# Revit family: Lighting-Troffer-Current-CBT2
name_source: partatom
category: Lighting Fixtures
units: mm (PartAtom-declared; Revit-internal decimal feet)

## family parameters
Cut with Voids When Loaded = No
Host = Face
Light Source = Yes
OmniClass Number = 23.80.70.11
OmniClass Title = Luminaries for Internal Lighting
Part Type = Normal
Room Calculation Point = No
Round Connector Dimension = Use Diameter
Shared = No

## types (1)
- Lighting-Troffer-Current-CBT2
    Apparent Load = 9 W
    Assembly Code = D5020200
    Color Filter = 16777215
    Color Rendering Index = 80
    Controller = Please Refer to the Product Spec Sheet for Control Options
    Default Elevation = 48 "
    Description = The CBT is a lensed troffer with switchable lumen and CCT options to create built-in versatility. Perfect for offices, classrooms and many other applications.
    Diffuser Material = Diffuser - Current - White
    Dimmimng Protocol = Dim-to-Off;0-10V;1%
    Dimming Lamp Color Temperature Shift = <None>
    Distribution Patterns = Lambertian
    Emit Shape Visible in Rendering = No
    Emit from Rectangle Length = 46 "
    Emit from Rectangle Width = 10 "
    Features = Switchable Lumen technology: 4400/3300/2750 lumens (1x4 and 2x2) 5500/4400/3300 lumens (2x4). Switchable CCT technology: 3500/4000/5000K. 1x4, 2x2, and 2x4 sizes. 0-10V 1% Dim to Off driver (standard) provides superior dimming capabilities. IC rated. Back-lit design and frosted lens provides smooth, even illumination across the face of the luminaire. All CBT LSCS Generation A units are priced as single units and must be ordered as single units in even quantities, as this product is packed two
fixtures per box.
    Housing Material = Paint - Current - White
    Installation and Service URL = https://cdn.currentlighting.com
    Lamp = LED
    Length = 48 "
    Load Classification = Lighting
    Manufacturer = Current Lighting
    Model = CBT
    Mounting = Please Refer to the Product Spec Sheet for Mounting Options
    Photometric Web File = CBT24_A_LSCS_EDD_2PK_5500lm_5000K.ies
    Photometry Note = Please Load IES File Listed Under Photometric Web File for Accurate Rendering
    Power Factor = 0.9
    Product Documentation Link = https://cdn.currentlighting.com
    Product Page URL = https://www.currentlighting.com
    Tilt Angle = -90.00°
    Type Comments = Light Fixture
    URL = https://www.currentlighting.com
    Voltage = 120 V
    Voltage Comments = 120 - 277V
    Wattage Comments = 24 - 48W
    Width = 12 "

## geometry (parser evidence)
native form markers: Sweep x1
no freeform markers — native parametric forms only
